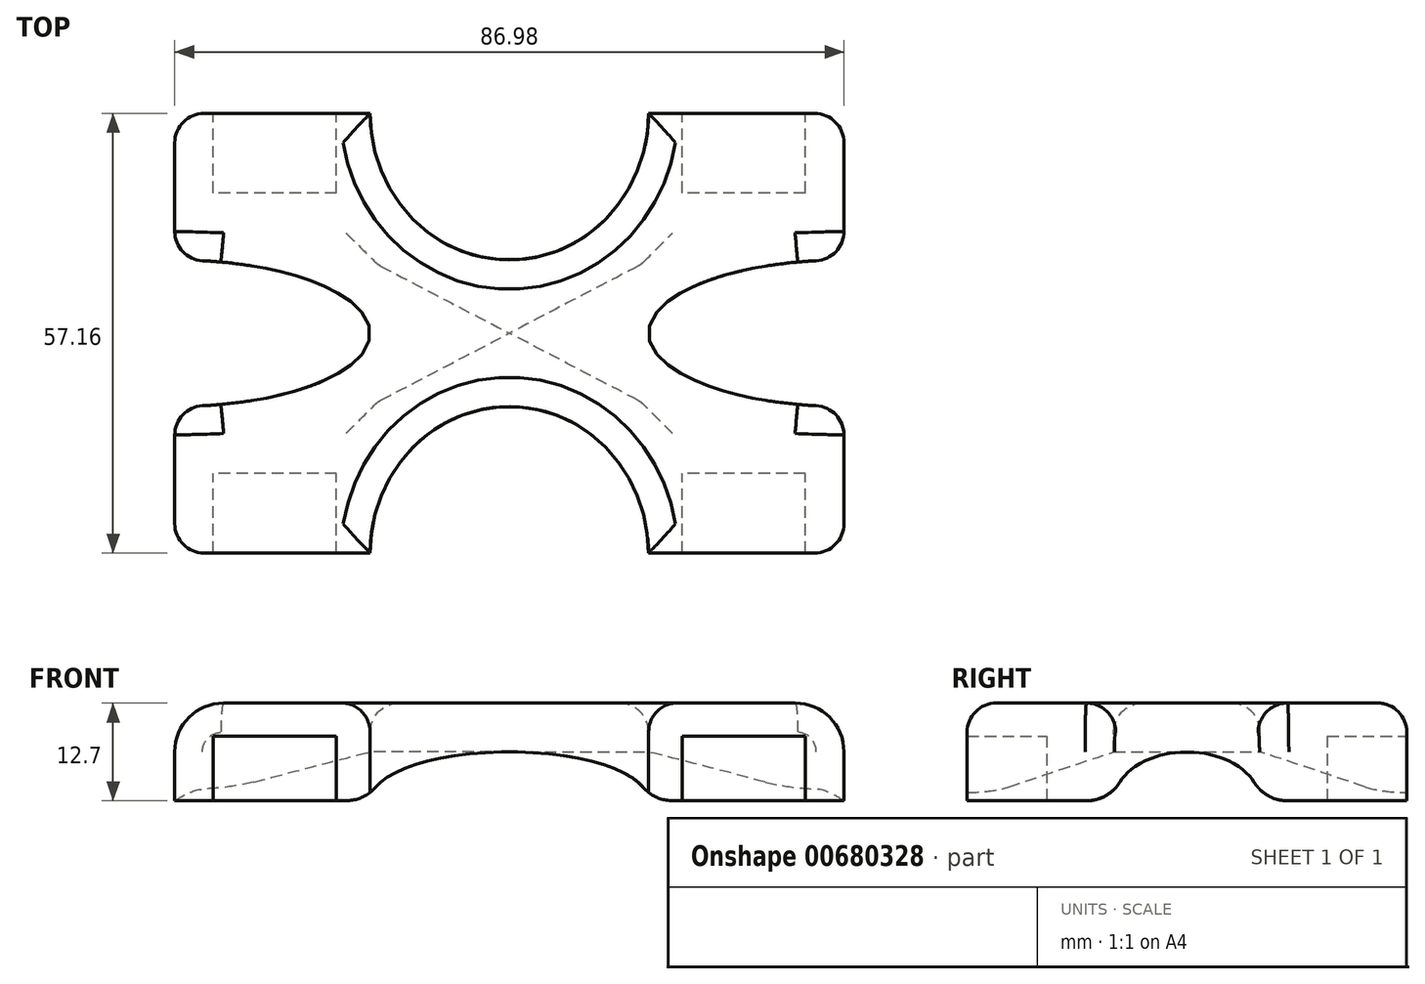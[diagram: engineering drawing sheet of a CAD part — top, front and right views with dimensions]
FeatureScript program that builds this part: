
annotation { "Feature Type Name" : "Feature", "Feature Type Description" : "" }
export const myFeature = defineFeature(function(context is Context, id is Id, definition is map)
    precondition{}
    {
        {
            var Q0;
            Q0=qCreatedBy(makeId("Top.planeOp"),FACE);
            var sketch = newSketch(context, id + "F0", { "sketchPlane" : qUnion([Q0])});
            skLineSegment(sketch, "E0.bottom", {"start": v(43.49, 28.57) * mm, "end": v(18.09, 28.57) * mm});
            skLineSegment(sketch, "E0.top", {"start": v(43.49, -28.58) * mm, "end": v(18.09, -28.58) * mm});
            skLineSegment(sketch, "E0.left", {"start": v(43.49, 28.58) * mm, "end": v(43.49, 22.22) * mm});
            skLineSegment(sketch, "E0.right", {"start": v(-43.49, 28.58) * mm, "end": v(-43.49, 9.52) * mm});
            skPoint(sketch, "E0.middle", {"position": v(0, 0) * mm});
            skEllipticalArc(sketch, "E1", {});
            skLineSegment(sketch, "E2", {"start": v(18.09, 28.58) * mm, "end": v(18.09, -28.58) * mm, "construction": true});
            skLineSegment(sketch, "E3", {"start": v(-18.09, 28.58) * mm, "end": v(-18.09, -28.58) * mm, "construction": true});
            skEllipticalArc(sketch, "E4", {});
            skLineSegment(sketch, "E5", {"start": v(43.49, -9.52) * mm, "end": v(-43.49, -9.53) * mm, "construction": true});
            skLineSegment(sketch, "E6", {"start": v(38.1, 9.53) * mm, "end": v(-43.49, 9.53) * mm, "construction": true});
            skLineSegment(sketch, "E7", {"start": v(43.49, -9.53) * mm, "end": v(-43.49, -9.53) * mm, "construction": true});
            skLineSegment(sketch, "E8", {"start": v(43.49, 9.53) * mm, "end": v(-43.49, 9.53) * mm, "construction": true});
            skEllipticalArc(sketch, "E9", {});
            skEllipticalArc(sketch, "E10", {});
            skLineSegment(sketch, "E11.trimOffspring", {"start": v(-43.49, -9.52) * mm, "end": v(-43.49, -28.58) * mm});
            skLineSegment(sketch, "E12.trimOffspring", {"start": v(-18.09, 28.57) * mm, "end": v(-43.49, 28.57) * mm});
            skLineSegment(sketch, "E13.trimOffspring", {"start": v(43.49, -9.53) * mm, "end": v(43.49, -28.58) * mm});
            skLineSegment(sketch, "E14.trimOffspring", {"start": v(-18.09, -28.58) * mm, "end": v(-43.49, -28.58) * mm});
            skLineSegment(sketch, "E15", {"start": v(43.49, 22.22) * mm, "end": v(43.49, 9.53) * mm});
            const initialGuessF0  = {"E1": [0, 0.028575, 1, 0, 0.018088521426076875, 0.01905, 3.141592653589793, 6.283185307179586], "E4": [0, -0.028575, 1, 0, 0.018088521426076875, 0.01905, 6.283185307179586, 3.141592653589793], "E9": [0.043488521426076884, 0, 0, -1, 0.009525, 0.0254, 3.141592653589793, 6.283185307179586], "E10": [-0.04348852142607689, 0, -6.380968387238897e-08, -1, 0.009525, 0.0254, 6.283185307179586, 3.141592653589793]};
            skSetInitialGuess(sketch, initialGuessF0);
            skSolve(sketch);
        }
        {
            var Q0;
            Q0 = qSketchRegion(id + "F0", true);
            extrude(context, id + "F1", {"entities" : qUnion([Q0]), "depth" : 12.7 * mm, "offsetDistance" : 25.4 * mm});
        }
        {
            var Q0;
            Q0=makeQuery(id+"F1.opExtrude","CAP_EDGE",EDGE,{"disambiguationData":[OSD([sQuery(id+"F0.wireOp",EDGE,"E13.trimOffspring")])],"isStart":false});
            var Q1;
            Q1=makeQuery(id+"F1.opExtrude","CAP_EDGE",EDGE,{"disambiguationData":[OSD([sQuery(id+"F0.wireOp",EDGE,"E0.left")])],"isStart":false});
            var Q2;
            Q2=makeQuery(id+"F1.opExtrude","CAP_EDGE",EDGE,{"disambiguationData":[OSD([sQuery(id+"F0.wireOp",EDGE,"E0.right")])],"isStart":false});
            var Q3;
            Q3=makeQuery(id+"F1.opExtrude","CAP_EDGE",EDGE,{"disambiguationData":[OSD([sQuery(id+"F0.wireOp",EDGE,"E11.trimOffspring")])],"isStart":false});
            fillet(context, id + "F2", {"entities" : qUnion([Q0, Q1, Q2, Q3]), "radius" : 6.35 * mm, "tangentPropagation" : true, "allowEdgeOverflow" : false});
        }
        {
            var Q0;
            Q0=makeQuery(id+"F1.opExtrude","CAP_FACE",FACE,{"disambiguationData":[OSD([sQuery(id+"F0.wireOp",EDGE,"E0.bottom"),sQuery(id+"F0.wireOp",EDGE,"E0.top"),sQuery(id+"F0.wireOp",EDGE,"E0.left"),sQuery(id+"F0.wireOp",EDGE,"E0.right"),sQuery(id+"F0.wireOp",EDGE,"E1"),sQuery(id+"F0.wireOp",EDGE,"E4"),sQuery(id+"F0.wireOp",EDGE,"E9"),sQuery(id+"F0.wireOp",EDGE,"E10"),sQuery(id+"F0.wireOp",EDGE,"E11.trimOffspring"),sQuery(id+"F0.wireOp",EDGE,"E12.trimOffspring"),sQuery(id+"F0.wireOp",EDGE,"E13.trimOffspring"),sQuery(id+"F0.wireOp",EDGE,"E14.trimOffspring")])],"isStart":false});
            fillet(context, id + "F3", {"entities" : qUnion([Q0]), "radius" : 3.8 * mm, "tangentPropagation" : true, "allowEdgeOverflow" : false});
        }
        {
            var Q0;
            Q0=makeQuery(id+"F1.opExtrude","CAP_FACE",FACE,{"disambiguationData":[OSD([sQuery(id+"F0.wireOp",EDGE,"E0.bottom"),sQuery(id+"F0.wireOp",EDGE,"E0.top"),sQuery(id+"F0.wireOp",EDGE,"E0.left"),sQuery(id+"F0.wireOp",EDGE,"E0.right"),sQuery(id+"F0.wireOp",EDGE,"E1"),sQuery(id+"F0.wireOp",EDGE,"E4"),sQuery(id+"F0.wireOp",EDGE,"E9"),sQuery(id+"F0.wireOp",EDGE,"E10"),sQuery(id+"F0.wireOp",EDGE,"E11.trimOffspring"),sQuery(id+"F0.wireOp",EDGE,"E12.trimOffspring"),sQuery(id+"F0.wireOp",EDGE,"E13.trimOffspring"),sQuery(id+"F0.wireOp",EDGE,"E14.trimOffspring"),sQuery(id+"F0.wireOp",EDGE,"E15")])],"isStart":true});
            var sketch = newSketch(context, id + "F4", { "sketchPlane" : qUnion([Q0])});
            skLineSegment(sketch, "E16.bottom", {"start": v(38.47, 38.91) * mm, "end": v(22.47, 38.91) * mm});
            skLineSegment(sketch, "E16.top", {"start": v(38.47, 18.24) * mm, "end": v(22.47, 18.24) * mm});
            skLineSegment(sketch, "E16.left", {"start": v(38.47, 38.91) * mm, "end": v(38.47, 18.24) * mm});
            skLineSegment(sketch, "E16.right", {"start": v(22.47, 38.91) * mm, "end": v(22.47, 18.24) * mm});
            skPoint(sketch, "E16.middle", {"position": v(30.47, 28.58) * mm});
            skLineSegment(sketch, "E17.bottom", {"start": v(38.47, -18.24) * mm, "end": v(22.47, -18.24) * mm});
            skLineSegment(sketch, "E17.top", {"start": v(38.47, -38.91) * mm, "end": v(22.47, -38.91) * mm});
            skLineSegment(sketch, "E17.left", {"start": v(38.47, -18.24) * mm, "end": v(38.47, -38.91) * mm});
            skLineSegment(sketch, "E17.right", {"start": v(22.47, -18.24) * mm, "end": v(22.47, -38.91) * mm});
            skPoint(sketch, "E17.middle", {"position": v(30.47, -28.57) * mm});
            skLineSegment(sketch, "E18.bottom", {"start": v(-22.47, 38.91) * mm, "end": v(-38.47, 38.91) * mm});
            skLineSegment(sketch, "E18.top", {"start": v(-22.47, 18.24) * mm, "end": v(-38.47, 18.24) * mm});
            skLineSegment(sketch, "E18.left", {"start": v(-22.47, 38.91) * mm, "end": v(-22.47, 18.24) * mm});
            skLineSegment(sketch, "E18.right", {"start": v(-38.47, 38.91) * mm, "end": v(-38.47, 18.24) * mm});
            skPoint(sketch, "E18.middle", {"position": v(-30.47, 28.58) * mm});
            skLineSegment(sketch, "E19.bottom", {"start": v(-22.47, -18.24) * mm, "end": v(-38.47, -18.24) * mm});
            skLineSegment(sketch, "E19.top", {"start": v(-22.47, -38.91) * mm, "end": v(-38.47, -38.91) * mm});
            skLineSegment(sketch, "E19.left", {"start": v(-22.47, -18.24) * mm, "end": v(-22.47, -38.91) * mm});
            skLineSegment(sketch, "E19.right", {"start": v(-38.47, -18.24) * mm, "end": v(-38.47, -38.91) * mm});
            skPoint(sketch, "E19.middle", {"position": v(-30.47, -28.57) * mm});
            skSolve(sketch);
        }
        {
            var Q0;
            {var subQ8=sQuery(id+"F4.wireOp",EDGE,"E16.top");Q0=makeQuery(id+"F4.imprint","IMPRINT",FACE,{"disambiguationData":[TD([[makeQuery(id+"F4.imprint","IMPRINT",EDGE,{"derivedFrom":subQ8}),-1.0]])]});}
            var Q1;
            {var subQ0=sQuery(id+"F4.wireOp",EDGE,"E18.top");Q1=makeQuery(id+"F4.imprint","IMPRINT",FACE,{"disambiguationData":[TD([[makeQuery(id+"F4.imprint","IMPRINT",EDGE,{"derivedFrom":subQ0}),-1.0]])]});}
            var Q2;
            {var subQ0=sQuery(id+"F4.wireOp",EDGE,"E19.bottom");Q2=makeQuery(id+"F4.imprint","IMPRINT",FACE,{"disambiguationData":[TD([[makeQuery(id+"F4.imprint","IMPRINT",EDGE,{"derivedFrom":subQ0}),1.0]])]});}
            var Q3;
            {var subQ0=sQuery(id+"F4.wireOp",EDGE,"E17.bottom");Q3=makeQuery(id+"F4.imprint","IMPRINT",FACE,{"disambiguationData":[TD([[makeQuery(id+"F4.imprint","IMPRINT",EDGE,{"derivedFrom":subQ0}),1.0]])]});}
            extrude(context, id + "F5", {"entities" : qUnion([Q0, Q1, Q2, Q3]), "operationType" : NewBodyOperationType.REMOVE, "oppositeDirection" : true, "depth" : 8.4 * mm, "offsetDistance" : 25.4 * mm});
        }
        {
            var Q0;
            Q0=makeQuery(id+"F1.opExtrude","SWEPT_FACE",FACE,{"disambiguationData":[OSD([sQuery(id+"F0.wireOp",EDGE,"E14.trimOffspring")])]});
            var sketch = newSketch(context, id + "F6", { "sketchPlane" : qUnion([Q0])});
            skPoint(sketch, "E20.0", {"position": v(-22.47, 0) * mm});
            skPoint(sketch, "E21.0", {"position": v(22.47, 0) * mm});
            skPoint(sketch, "E22.0", {"position": v(-18.09, 0) * mm});
            skPoint(sketch, "E23.0", {"position": v(18.09, 0) * mm});
            skEllipse(sketch, "E24", {"center": v(0, 0) * mm, "majorRadius": 18.09 * mm, "minorRadius": 6.35 * mm, "majorAxis": v(1, 0)});
            skSolve(sketch);
        }
        {
            var Q0;
            Q0=makeQuery(id+"F6.imprint","IMPRINT",FACE,{"disambiguationData":[TD([[makeQuery(id+"F6.imprint","IMPRINT",EDGE,{"derivedFrom":sQuery(id+"F6.wireOp",EDGE,"E24")}),1.0]])]});
            extrude(context, id + "F7", {"entities" : qUnion([Q0]), "operationType" : NewBodyOperationType.REMOVE, "endBound" : BoundingType.THROUGH_ALL, "oppositeDirection" : true, "depth" : 25.4 * mm, "offsetDistance" : 25.4 * mm});
        }
        {
            var Q0;
            Q0=makeQuery(id+"F1.opExtrude","SWEPT_FACE",FACE,{"disambiguationData":[OSD([sQuery(id+"F0.wireOp",EDGE,"E0.left"),sQuery(id+"F0.wireOp",EDGE,"E15")])]});
            var sketch = newSketch(context, id + "F8", { "sketchPlane" : qUnion([Q0])});
            skPoint(sketch, "E25.0", {"position": v(-9.43, 0) * mm});
            skPoint(sketch, "E26.0", {"position": v(9.43, 0) * mm});
            skEllipse(sketch, "E27", {"center": v(0, 0) * mm, "majorRadius": 9.43 * mm, "minorRadius": 6.35 * mm, "majorAxis": v(1, 0)});
            skSolve(sketch);
        }
        {
            var Q0;
            Q0 = qSketchRegion(id + "F8", true);
            extrude(context, id + "F9", {"entities" : qUnion([Q0]), "operationType" : NewBodyOperationType.REMOVE, "endBound" : BoundingType.THROUGH_ALL, "oppositeDirection" : true, "depth" : 25.4 * mm, "offsetDistance" : 25.4 * mm});
        }
        {
            var Q0;
            {var subQ0=sQuery(id+"F0.wireOp",EDGE,"E13.trimOffspring");var subQ1=sQuery(id+"F0.wireOp",EDGE,"E9");var subQ2=sQuery(id+"F0.wireOp",EDGE,"E4");var subQ3=sQuery(id+"F0.wireOp",EDGE,"E0.top");var subQ4=makeQuery(id+"F1.opExtrude","CAP_FACE",FACE,{"disambiguationData":[OSD([sQuery(id+"F0.wireOp",EDGE,"E0.bottom"),subQ3,sQuery(id+"F0.wireOp",EDGE,"E0.left"),sQuery(id+"F0.wireOp",EDGE,"E0.right"),sQuery(id+"F0.wireOp",EDGE,"E1"),subQ2,subQ1,sQuery(id+"F0.wireOp",EDGE,"E10"),sQuery(id+"F0.wireOp",EDGE,"E11.trimOffspring"),sQuery(id+"F0.wireOp",EDGE,"E12.trimOffspring"),subQ0,sQuery(id+"F0.wireOp",EDGE,"E14.trimOffspring"),sQuery(id+"F0.wireOp",EDGE,"E15")])],"isStart":true});Q0=makeQuery(id+"F9.boolean.opBoolean","INTERSECT",EDGE,{"derivedFrom":[makeQuery(id+"F7.boolean.opBoolean","SPLIT",FACE,{"disambiguationData":[TD([makeQuery(id+"F1.opExtrude","SWEPT_FACE",FACE,{"disambiguationData":[OSD([subQ3])]})])],"derivedFrom":subQ4}),makeQuery(id+"F9.opExtrude","SWEPT_FACE",FACE,{"disambiguationData":[OSD([sQuery(id+"F8.wireOp",EDGE,"E27")])]})]});}
            var Q1;
            Q1=makeQuery(id+"F7.boolean.opBoolean","INTERSECT",EDGE,{"disambiguationData":[OD(1.0)],"derivedFrom":[makeQuery(id+"F1.opExtrude","CAP_FACE",FACE,{"disambiguationData":[OSD([sQuery(id+"F0.wireOp",EDGE,"E0.bottom"),sQuery(id+"F0.wireOp",EDGE,"E0.top"),sQuery(id+"F0.wireOp",EDGE,"E0.left"),sQuery(id+"F0.wireOp",EDGE,"E0.right"),sQuery(id+"F0.wireOp",EDGE,"E1"),sQuery(id+"F0.wireOp",EDGE,"E4"),sQuery(id+"F0.wireOp",EDGE,"E9"),sQuery(id+"F0.wireOp",EDGE,"E10"),sQuery(id+"F0.wireOp",EDGE,"E11.trimOffspring"),sQuery(id+"F0.wireOp",EDGE,"E12.trimOffspring"),sQuery(id+"F0.wireOp",EDGE,"E13.trimOffspring"),sQuery(id+"F0.wireOp",EDGE,"E14.trimOffspring"),sQuery(id+"F0.wireOp",EDGE,"E15")])],"isStart":true}),makeQuery(id+"F7.opExtrude","SWEPT_FACE",FACE,{"disambiguationData":[OSD([sQuery(id+"F6.wireOp",EDGE,"E24")])]})]});
            var Q2;
            Q2=makeQuery(id+"F7.boolean.opBoolean","INTERSECT",EDGE,{"disambiguationData":[OD(0.0)],"derivedFrom":[makeQuery(id+"F1.opExtrude","CAP_FACE",FACE,{"disambiguationData":[OSD([sQuery(id+"F0.wireOp",EDGE,"E0.bottom"),sQuery(id+"F0.wireOp",EDGE,"E0.top"),sQuery(id+"F0.wireOp",EDGE,"E0.left"),sQuery(id+"F0.wireOp",EDGE,"E0.right"),sQuery(id+"F0.wireOp",EDGE,"E1"),sQuery(id+"F0.wireOp",EDGE,"E4"),sQuery(id+"F0.wireOp",EDGE,"E9"),sQuery(id+"F0.wireOp",EDGE,"E10"),sQuery(id+"F0.wireOp",EDGE,"E11.trimOffspring"),sQuery(id+"F0.wireOp",EDGE,"E12.trimOffspring"),sQuery(id+"F0.wireOp",EDGE,"E13.trimOffspring"),sQuery(id+"F0.wireOp",EDGE,"E14.trimOffspring"),sQuery(id+"F0.wireOp",EDGE,"E15")])],"isStart":true}),makeQuery(id+"F7.opExtrude","SWEPT_FACE",FACE,{"disambiguationData":[OSD([sQuery(id+"F6.wireOp",EDGE,"E24")])]})]});
            var Q3;
            {var subQ0=sQuery(id+"F0.wireOp",EDGE,"E15");var subQ1=sQuery(id+"F0.wireOp",EDGE,"E9");var subQ2=sQuery(id+"F0.wireOp",EDGE,"E1");var subQ3=sQuery(id+"F0.wireOp",EDGE,"E0.left");var subQ4=sQuery(id+"F0.wireOp",EDGE,"E0.bottom");var subQ5=makeQuery(id+"F1.opExtrude","CAP_FACE",FACE,{"disambiguationData":[OSD([subQ4,sQuery(id+"F0.wireOp",EDGE,"E0.top"),subQ3,sQuery(id+"F0.wireOp",EDGE,"E0.right"),subQ2,sQuery(id+"F0.wireOp",EDGE,"E4"),subQ1,sQuery(id+"F0.wireOp",EDGE,"E10"),sQuery(id+"F0.wireOp",EDGE,"E11.trimOffspring"),sQuery(id+"F0.wireOp",EDGE,"E12.trimOffspring"),sQuery(id+"F0.wireOp",EDGE,"E13.trimOffspring"),sQuery(id+"F0.wireOp",EDGE,"E14.trimOffspring"),subQ0])],"isStart":true});Q3=makeQuery(id+"F9.boolean.opBoolean","INTERSECT",EDGE,{"derivedFrom":[makeQuery(id+"F7.boolean.opBoolean","SPLIT",FACE,{"disambiguationData":[TD([makeQuery(id+"F1.opExtrude","SWEPT_FACE",FACE,{"disambiguationData":[OSD([subQ4])]})])],"derivedFrom":subQ5}),makeQuery(id+"F9.opExtrude","SWEPT_FACE",FACE,{"disambiguationData":[OSD([sQuery(id+"F8.wireOp",EDGE,"E27")])]})]});}
            var Q4;
            Q4=makeQuery(id+"F7.boolean.opBoolean","INTERSECT",EDGE,{"disambiguationData":[OD(2.0)],"derivedFrom":[makeQuery(id+"F1.opExtrude","CAP_FACE",FACE,{"disambiguationData":[OSD([sQuery(id+"F0.wireOp",EDGE,"E0.bottom"),sQuery(id+"F0.wireOp",EDGE,"E0.top"),sQuery(id+"F0.wireOp",EDGE,"E0.left"),sQuery(id+"F0.wireOp",EDGE,"E0.right"),sQuery(id+"F0.wireOp",EDGE,"E1"),sQuery(id+"F0.wireOp",EDGE,"E4"),sQuery(id+"F0.wireOp",EDGE,"E9"),sQuery(id+"F0.wireOp",EDGE,"E10"),sQuery(id+"F0.wireOp",EDGE,"E11.trimOffspring"),sQuery(id+"F0.wireOp",EDGE,"E12.trimOffspring"),sQuery(id+"F0.wireOp",EDGE,"E13.trimOffspring"),sQuery(id+"F0.wireOp",EDGE,"E14.trimOffspring"),sQuery(id+"F0.wireOp",EDGE,"E15")])],"isStart":true}),makeQuery(id+"F7.opExtrude","SWEPT_FACE",FACE,{"disambiguationData":[OSD([sQuery(id+"F6.wireOp",EDGE,"E24")])]})]});
            var Q5;
            {var subQ0=sQuery(id+"F0.wireOp",EDGE,"E12.trimOffspring");var subQ1=sQuery(id+"F0.wireOp",EDGE,"E0.right");var subQ2=sQuery(id+"F0.wireOp",EDGE,"E10");var subQ3=sQuery(id+"F0.wireOp",EDGE,"E1");var subQ4=makeQuery(id+"F1.opExtrude","CAP_FACE",FACE,{"disambiguationData":[OSD([sQuery(id+"F0.wireOp",EDGE,"E0.bottom"),sQuery(id+"F0.wireOp",EDGE,"E0.top"),sQuery(id+"F0.wireOp",EDGE,"E0.left"),subQ1,subQ3,sQuery(id+"F0.wireOp",EDGE,"E4"),sQuery(id+"F0.wireOp",EDGE,"E9"),subQ2,sQuery(id+"F0.wireOp",EDGE,"E11.trimOffspring"),subQ0,sQuery(id+"F0.wireOp",EDGE,"E13.trimOffspring"),sQuery(id+"F0.wireOp",EDGE,"E14.trimOffspring"),sQuery(id+"F0.wireOp",EDGE,"E15")])],"isStart":true});Q5=makeQuery(id+"F9.boolean.opBoolean","INTERSECT",EDGE,{"derivedFrom":[makeQuery(id+"F7.boolean.opBoolean","SPLIT",FACE,{"disambiguationData":[TD([makeQuery(id+"F1.opExtrude","SWEPT_FACE",FACE,{"disambiguationData":[OSD([subQ1])]})])],"derivedFrom":subQ4}),makeQuery(id+"F9.opExtrude","SWEPT_FACE",FACE,{"disambiguationData":[OSD([sQuery(id+"F8.wireOp",EDGE,"E27")])]})]});}
            var Q6;
            Q6=makeQuery(id+"F7.boolean.opBoolean","INTERSECT",EDGE,{"disambiguationData":[OD(3.0)],"derivedFrom":[makeQuery(id+"F1.opExtrude","CAP_FACE",FACE,{"disambiguationData":[OSD([sQuery(id+"F0.wireOp",EDGE,"E0.bottom"),sQuery(id+"F0.wireOp",EDGE,"E0.top"),sQuery(id+"F0.wireOp",EDGE,"E0.left"),sQuery(id+"F0.wireOp",EDGE,"E0.right"),sQuery(id+"F0.wireOp",EDGE,"E1"),sQuery(id+"F0.wireOp",EDGE,"E4"),sQuery(id+"F0.wireOp",EDGE,"E9"),sQuery(id+"F0.wireOp",EDGE,"E10"),sQuery(id+"F0.wireOp",EDGE,"E11.trimOffspring"),sQuery(id+"F0.wireOp",EDGE,"E12.trimOffspring"),sQuery(id+"F0.wireOp",EDGE,"E13.trimOffspring"),sQuery(id+"F0.wireOp",EDGE,"E14.trimOffspring"),sQuery(id+"F0.wireOp",EDGE,"E15")])],"isStart":true}),makeQuery(id+"F7.opExtrude","SWEPT_FACE",FACE,{"disambiguationData":[OSD([sQuery(id+"F6.wireOp",EDGE,"E24")])]})]});
            var Q7;
            {var subQ0=sQuery(id+"F0.wireOp",EDGE,"E14.trimOffspring");var subQ1=sQuery(id+"F0.wireOp",EDGE,"E11.trimOffspring");var subQ2=sQuery(id+"F0.wireOp",EDGE,"E10");var subQ3=sQuery(id+"F0.wireOp",EDGE,"E4");var subQ4=makeQuery(id+"F1.opExtrude","CAP_FACE",FACE,{"disambiguationData":[OSD([sQuery(id+"F0.wireOp",EDGE,"E0.bottom"),sQuery(id+"F0.wireOp",EDGE,"E0.top"),sQuery(id+"F0.wireOp",EDGE,"E0.left"),sQuery(id+"F0.wireOp",EDGE,"E0.right"),sQuery(id+"F0.wireOp",EDGE,"E1"),subQ3,sQuery(id+"F0.wireOp",EDGE,"E9"),subQ2,subQ1,sQuery(id+"F0.wireOp",EDGE,"E12.trimOffspring"),sQuery(id+"F0.wireOp",EDGE,"E13.trimOffspring"),subQ0,sQuery(id+"F0.wireOp",EDGE,"E15")])],"isStart":true});Q7=makeQuery(id+"F9.boolean.opBoolean","INTERSECT",EDGE,{"derivedFrom":[makeQuery(id+"F7.boolean.opBoolean","SPLIT",FACE,{"disambiguationData":[TD([makeQuery(id+"F1.opExtrude","SWEPT_FACE",FACE,{"disambiguationData":[OSD([subQ1])]})])],"derivedFrom":subQ4}),makeQuery(id+"F9.opExtrude","SWEPT_FACE",FACE,{"disambiguationData":[OSD([sQuery(id+"F8.wireOp",EDGE,"E27")])]})]});}
            fillet(context, id + "F10", {"entities" : qUnion([Q0, Q1, Q2, Q3, Q4, Q5, Q6, Q7]), "radius" : 5.08 * mm, "tangentPropagation" : true, "allowEdgeOverflow" : false});
        }
    });
